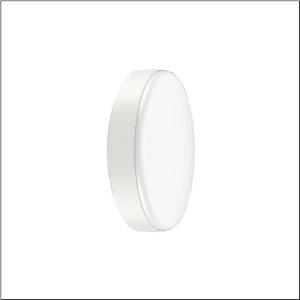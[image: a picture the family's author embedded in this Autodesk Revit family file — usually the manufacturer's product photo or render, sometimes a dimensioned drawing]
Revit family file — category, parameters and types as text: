
# Revit family: rondel_31_51wc10mb44as
name_source: partatom
category: Lighting Fixtures
units: mm (PartAtom-declared; Revit-internal decimal feet)

## family parameters
Cut with Voids When Loaded = No
Host = Face
Light Source = No
Part Type = Normal
Room Calculation Point = No
Round Connector Dimension = Use Diameter
Shared = No

## types (1)
- --- (1 x LED, 4400 lm, 35.5 W, 4000K)
    Apparent Load = 36 VA
    CIE Flux Codes = 44 75 94 94 100
    Color Rendering = 80
    Color Temperature = 4000K
    Default Elevation = 1800 mm
    Description = Rondel 31, wall and ceiling luminaire, primary optical cover: cover, of PC, opal, light emission: direct distribution, primary light characteristic: symmetric, installation type: surface-mounted, LED, rated luminous flux: 4.400lm, luminous efficacy: 124lm/W, light colour: 840, colour temperature: 4000K, with terminal, 3-pole, max. 2.5mm², mains connection: 220..240V, AC, 50/60Hz, rated input power: 35.5W, luminaire housing, of PC, traffic white (RAL 9016), diameter: 480mm, brightness and presence sensor, HF sensor, protection rating (complete): IP65, insulation class (complete): insulation class II (safety insulation), certification: CE, impact resistance: IK10, permissible operating ambient temperature: -20..+40°C, permissible storage temperature: -20..+60°C, packaging unit: 1 piece
    Height = 97 mm
    Lamp = 1 x LED
    Lamp Light Flux = 4400 lm
    Lamp Power = 35.5 W
    Lamp count = 1
    Length = 480 mm
    Luminous efficacy = 124 lm/W
    Manufacturer = Siteco
    ModVariant = No
    Model = 51WC10MB44AS
    Mounting Place = Ceiling
    Mounting Type = Surface mounted
    Number of Poles = 1
    OnlyDefault = Yes
    Power Factor = 1
    Product Name = Rondel 31
    Product group = wall and ceiling luminaire
    ProductGroupID = 302
    Protection Class = Protection class II
    Protection Degree = IP 65
    RLX_Detail_Level = 1
    RLX_Emergency_Light_Flux = 0 lm
    RLX_Emergency_Type = 0
    RLX_Emergency_Type_DB = No
    RlxData = <blob elided: 41493 chars, md5=e0294f07>
    Socket = socket
    Standby Power = 0 W
    System Light Flux = 4400 lm
    System Power = 36 W
    Type Comments = factory setting: luminous flux: 100 % | (ON | ON)
    Type Image = l_1007188.jpg
    URL = http://relux.com
    VarID = @adj_100985
    Voltage = 0 V
    Weight = 0.00 kg
    Width = 0 mm  [stored 0 ft]

note: [stored X ft] marks values corroborated as IEEE doubles in the binary element streams (Revit-internal decimal feet)

## geometry (parser evidence)
native form markers: Blend x4, Sweep x11
no freeform markers — native parametric forms only
